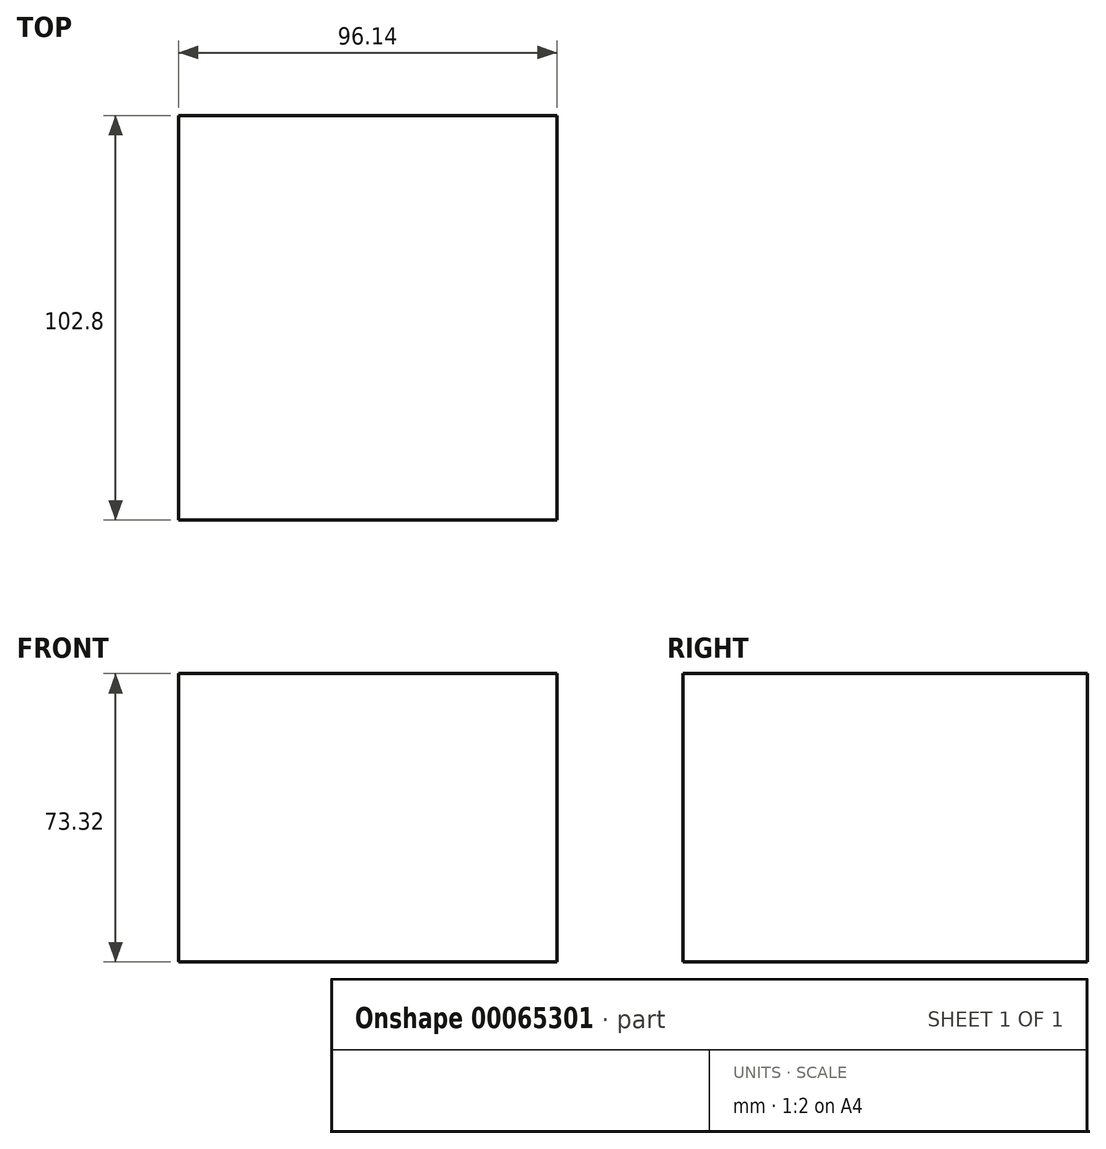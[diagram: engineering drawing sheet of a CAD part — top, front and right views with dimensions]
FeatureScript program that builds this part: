
annotation { "Feature Type Name" : "Feature", "Feature Type Description" : "" }
export const myFeature = defineFeature(function(context is Context, id is Id, definition is map)
    precondition{}
    {
        {
            var Q0;
            Q0=qCreatedBy(makeId("Top.planeOp"),FACE);
            var sketch = newSketch(context, id + "F0", { "sketchPlane" : qUnion([Q0])});
            skLineSegment(sketch, "E0.rect.bottom", {"start": v(48.07, -51.4) * mm, "end": v(-48.07, -51.4) * mm});
            skLineSegment(sketch, "E0.rect.top", {"start": v(48.07, 51.4) * mm, "end": v(-48.07, 51.4) * mm});
            skLineSegment(sketch, "E0.rect.left", {"start": v(48.07, -51.4) * mm, "end": v(48.07, 51.4) * mm});
            skLineSegment(sketch, "E0.rect.right", {"start": v(-48.07, -51.4) * mm, "end": v(-48.07, 51.4) * mm});
            skPoint(sketch, "E0.rect.middle", {"position": v(0, 0) * mm});
            skSolve(sketch);
        }
        {
            var Q0;
            Q0 = qSketchRegion(id + "F0", true);
            extrude(context, id + "F1", {"entities" : qUnion([Q0]), "depth" : 73.32 * mm});
        }
    });
